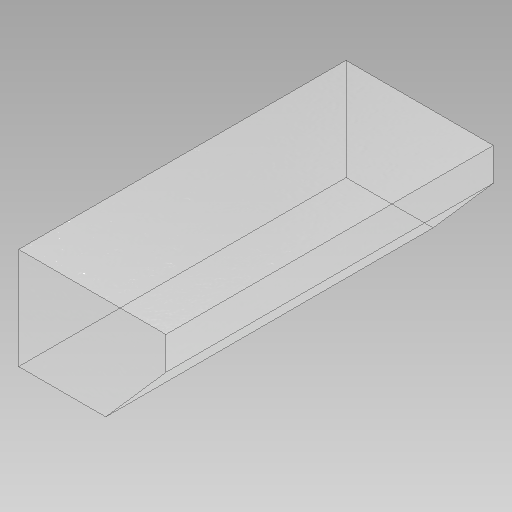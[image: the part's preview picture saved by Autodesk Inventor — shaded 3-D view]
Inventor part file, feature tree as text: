
AUTODESK INVENTOR PART (.ipt)
format: ipt  version: 2020 (Build 240168000, 168)  size: 176,128 bytes
history: native  units: in
note: dims shown in document units (in); Inventor stores cm internally (conversion verified against a paired STEP export)
features: extrude x5, sketch x4
ambient origin geometry x8: Origin, YZ Plane, XZ Plane, XY Plane, X Axis, Y Axis, Z Axis, Center Point
bodies: Solid1 (feature_tree)
feature tree (9):
  extrude  "Extrusion1"  Depth=7.874in
  extrude  "Extrusion2"  Depth=2.4409in
  extrude  "Extrusion3"  TaperAngle=90.0deg  [1 undecoded]
  sketch  "Sketch4"  dims[d7=2.4409in d8=0.0in d9=0.7874in d10=2.3622in d11=120.0deg d12=0.7874in d13=2.3622in d14=120.0deg d15=2.4409in d16=0.0in d17=2.4409in d18=0.0in d19=2.4409in d20=0.0in]
  extrude  "Extrusion4"  Depth=2.4409in
  extrude  "Extrusion5"  Depth=2.4409in
  sketch  "Sketch1"  dims[d0=1.9685in d1=7.874in]
  sketch  "Sketch2"  dims[d2=2.4409in d3=0.0in d4=1.5748in]
  sketch  "Sketch3"  dims[d5=0.7874in d6=90.0deg]
note: 1 required parameter value undecoded (feature->parameter linkage not recoverable at this tier; creation-order binding heuristic only, values carry confidence <= 0.55)
